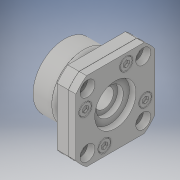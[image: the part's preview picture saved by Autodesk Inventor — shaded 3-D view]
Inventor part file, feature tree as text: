
AUTODESK INVENTOR PART (.ipt)
format: ipt  version: 2019 (Build 230136000, 136)  size: 324,096 bytes
history: native  units: mm
features: other x28, sketch x7, revolve x4, extrude x4, pattern_linear x3, hole x1
ambient origin geometry x8: Origin, YZ Plane, XZ Plane, XY Plane, X Axis, Y Axis, Z Axis, Center Point
bodies: Solid1 (feature_tree)
feature tree (47):
  revolve  "Revolution1"  [1 undecoded]
  extrude  "Extrusion1"  TaperAngle=360.0deg  [1 undecoded]
  revolve  "Revolution2"  [1 undecoded]
  revolve  "Revolution3"  [1 undecoded]
  revolve  "Revolution4"  [1 undecoded]
  hole  "Hole1"  [1 undecoded]
  pattern_linear  "Rectangular Pattern1"  [2 undecoded]
  extrude  "Extrusion2"  [1 undecoded]
  extrude  "Extrusion3"  [1 undecoded]
  pattern_linear  "Rectangular Pattern2"  [2 undecoded]
  extrude  "Extrusion4"  [1 undecoded]
  pattern_linear  "Rectangular Pattern3"  [2 undecoded]
  other  "_to_bjs_XY"
  other  "_to_bjs_YZ"
  other  "_to_bjs_ZX"
  other  "_to_bjs_X"
  other  "_to_bjs_Y"
  other  "_to_bjs_Z"
  other  "_to_bjs_Center"
  other  "to_collar_XY"
  other  "to_collar_YZ"
  other  "to_collar_ZX"
  other  "to_collar_X"
  other  "to_collar_Y"
  other  "to_collar_Z"
  other  "to_collar_Center"
  other  "to_collar_2_XY"
  other  "to_collar_2_YZ"
  other  "to_collar_2_ZX"
  other  "to_collar_2_X"
  other  "to_collar_2_Y"
  other  "to_collar_2_Z"
  other  "to_collar_2_Center"
  other  "to_dummy_XY"
  other  "to_dummy_YZ"
  other  "to_dummy_ZX"
  other  "to_dummy_X"
  other  "to_dummy_Y"
  other  "to_dummy_Z"
  other  "to_dummy_Center"
  sketch  "Sketch_1"  dims[d0=360.0deg d1=10.0mm d2=0.0mm]
  sketch  "Sketch_2"  dims[d3=360.0deg d4=360.0deg]
  sketch  "Sketch_5"  dims[d5=360.0deg]
  sketch  "Sketch6"  dims[d6=4.5mm d7=6.0mm d8=8.0mm d9=4.0mm d10=90.0deg d11=10.0mm d12=0.0mm d13=20.0mm d15=29.698485mm d16=20.0mm d18=29.698485mm]
  sketch  "Sketch_9"  dims[d19=0.05mm d20=0.0mm d21=1.0mm d22=0.0mm]
  sketch  "Sketch_10"  dims[d23=20.0mm d25=24.041631mm d26=20.0mm d28=24.041631mm d29=1.0mm d30=0.0mm]
  sketch  "Sketch_12"  dims[d31=20.0mm d33=24.041631mm d34=20.0mm d36=24.041631mm d37=0.0mm d38=0.0mm d39=0.0mm d40=0.0mm]
note: 15 required parameter values undecoded (feature->parameter linkage not recoverable at this tier; creation-order binding heuristic only, values carry confidence <= 0.55)